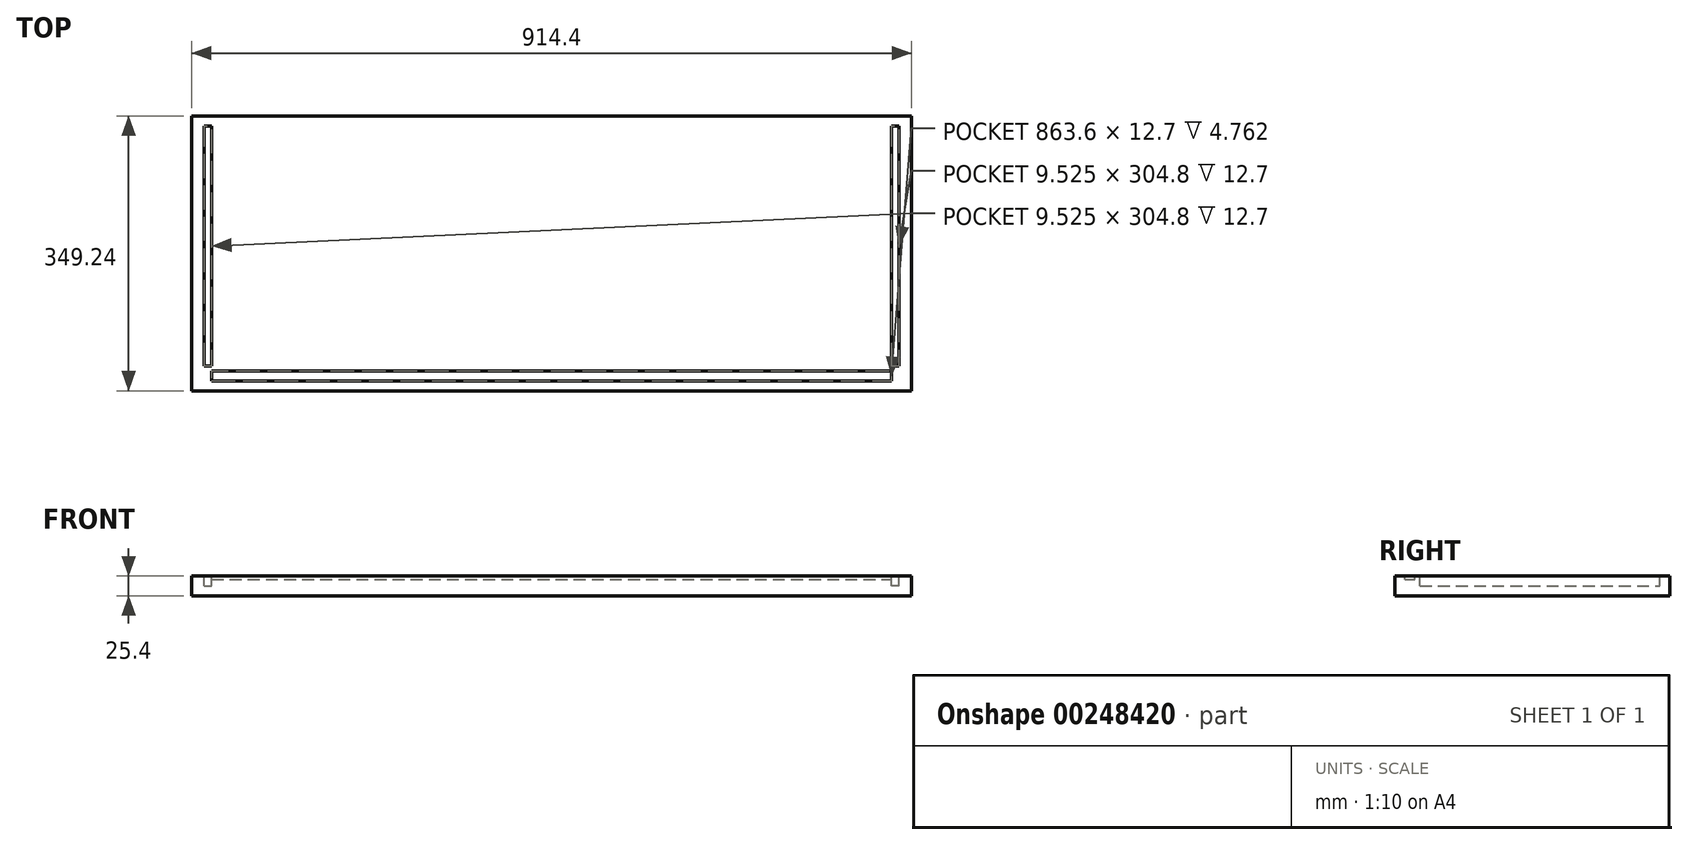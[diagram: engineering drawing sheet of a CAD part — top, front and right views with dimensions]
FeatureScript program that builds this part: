
annotation { "Feature Type Name" : "Feature", "Feature Type Description" : "" }
export const myFeature = defineFeature(function(context is Context, id is Id, definition is map)
    precondition{}
    {
        {
            var Q0;
            Q0=qCreatedBy(makeId("Top.planeOp"),FACE);
            var sketch = newSketch(context, id + "F0", { "sketchPlane" : qUnion([Q0])});
            skLineSegment(sketch, "E0.bottom", {"start": v(-457.2, 174.63) * mm, "end": v(457.2, 174.63) * mm});
            skLineSegment(sketch, "E0.top", {"start": v(-457.2, -174.63) * mm, "end": v(457.2, -174.63) * mm});
            skLineSegment(sketch, "E0.left", {"start": v(-457.2, 174.63) * mm, "end": v(-457.2, -174.63) * mm});
            skLineSegment(sketch, "E0.right", {"start": v(457.2, 174.63) * mm, "end": v(457.2, -174.63) * mm});
            skPoint(sketch, "E0.middle", {"position": v(0, 0) * mm});
            skSolve(sketch);
        }
        {
            var Q0;
            Q0 = qSketchRegion(id + "F0", true);
            extrude(context, id + "F1", {"entities" : qUnion([Q0]), "endBound" : BoundingType.SYMMETRIC, "depth" : 25.4 * mm});
        }
        {
            var Q0;
            Q0=makeQuery(id+"F1.opExtrude","CAP_FACE",FACE,{"disambiguationData":[OSD([sQuery(id+"F0.wireOp",EDGE,"E0.bottom"),sQuery(id+"F0.wireOp",EDGE,"E0.top"),sQuery(id+"F0.wireOp",EDGE,"E0.left"),sQuery(id+"F0.wireOp",EDGE,"E0.right")])],"isStart":false});
            var sketch = newSketch(context, id + "F2", { "sketchPlane" : qUnion([Q0])});
            skLineSegment(sketch, "E1", {"start": v(-431.8, -161.93) * mm, "end": v(431.8, -161.93) * mm});
            skLineSegment(sketch, "E2", {"start": v(-431.8, -149.23) * mm, "end": v(431.8, -149.23) * mm});
            skLineSegment(sketch, "E3", {"start": v(-431.8, -161.93) * mm, "end": v(-431.8, -149.23) * mm});
            skLineSegment(sketch, "E4", {"start": v(431.8, -161.93) * mm, "end": v(431.8, -149.23) * mm});
            skPoint(sketch, "E5.orphan", {"position": v(-457.2, -161.93) * mm});
            skPoint(sketch, "E6.orphan", {"position": v(-457.2, -149.23) * mm});
            skPoint(sketch, "E7.orphan", {"position": v(457.2, -149.23) * mm});
            skSolve(sketch);
        }
        {
            var Q0;
            Q0=makeQuery(id+"F2.imprint","IMPRINT",FACE,{"disambiguationData":[TD([[makeQuery(id+"F2.imprint","IMPRINT",EDGE,{"derivedFrom":sQuery(id+"F2.wireOp",EDGE,"E1")}),1.0]])]});
            extrude(context, id + "F3", {"entities" : qUnion([Q0]), "operationType" : NewBodyOperationType.REMOVE, "oppositeDirection" : true, "depth" : 4.76 * mm});
        }
        {
            var Q0;
            Q0=makeQuery(id+"F1.opExtrude","CAP_FACE",FACE,{"disambiguationData":[OSD([sQuery(id+"F0.wireOp",EDGE,"E0.bottom"),sQuery(id+"F0.wireOp",EDGE,"E0.top"),sQuery(id+"F0.wireOp",EDGE,"E0.left"),sQuery(id+"F0.wireOp",EDGE,"E0.right")])],"isStart":false});
            var sketch = newSketch(context, id + "F4", { "sketchPlane" : qUnion([Q0])});
            skLineSegment(sketch, "E8", {"start": v(-431.8, -142.88) * mm, "end": v(-431.8, 161.93) * mm});
            skLineSegment(sketch, "E9", {"start": v(-441.33, -142.88) * mm, "end": v(-441.33, 161.93) * mm});
            skLineSegment(sketch, "E10", {"start": v(-441.33, 161.93) * mm, "end": v(-431.8, 161.93) * mm});
            skLineSegment(sketch, "E11", {"start": v(-431.8, -142.88) * mm, "end": v(-441.33, -142.88) * mm});
            skPoint(sketch, "E12.orphan", {"position": v(-431.8, -174.63) * mm});
            skLineSegment(sketch, "E13.MirrorCS", {"start": v(431.8, -142.88) * mm, "end": v(431.8, 161.93) * mm});
            skLineSegment(sketch, "E14.MirrorCS", {"start": v(441.33, -142.88) * mm, "end": v(441.33, 161.93) * mm});
            skLineSegment(sketch, "E15.MirrorCS", {"start": v(441.33, 161.93) * mm, "end": v(431.8, 161.93) * mm});
            skLineSegment(sketch, "E16.MirrorCS", {"start": v(431.8, -142.88) * mm, "end": v(441.33, -142.88) * mm});
            skSolve(sketch);
        }
        {
            var Q0;
            Q0=makeQuery(id+"F4.imprint","IMPRINT",FACE,{"disambiguationData":[TD([[makeQuery(id+"F4.imprint","IMPRINT",EDGE,{"derivedFrom":sQuery(id+"F4.wireOp",EDGE,"E8")}),1.0]])]});
            var Q1;
            Q1=makeQuery(id+"F4.imprint","IMPRINT",FACE,{"disambiguationData":[TD([[makeQuery(id+"F4.imprint","IMPRINT",EDGE,{"derivedFrom":sQuery(id+"F4.wireOp",EDGE,"E13.MirrorCS")}),-1.0]])]});
            extrude(context, id + "F5", {"entities" : qUnion([Q0, Q1]), "operationType" : NewBodyOperationType.REMOVE, "oppositeDirection" : true, "depth" : 12.7 * mm});
        }
    });
